# Revit family: Regadera H-3301-CG
name_source: partatom
category: Plumbing Fixtures
revit_build: Autodesk Revit 2015 (Build: 20140223_1515(x64)
units: mm (PartAtom-declared; Revit-internal decimal feet)

## types (1)
- H-3301-C/G
    Ancho = 6.8 "
    Consumo Maximo = 10 l/min
    Default Elevation = 0.5 "
    Description = Regadera redonda de plato ancho, multichorro 7" de 6 chorros.
    Diametro Soporte Base = 2.2 "
    Garantía = El producto HELVEX esta garantizado como libre de defectos en materiales y procesos de fabricacion. El producto HELVEX esta garantizado , en lo que se refiere a los acabados; por un periodo de 10 años en los acabados cromo y duravex, y por 2 años en acabados diferentes al cromo, a partir de la fecha de compra indicada en la factura.
    Largo = 5.3 "
    Manufacturer = HELVEX S.A. DE C.V.
    Material = Brass Chromed
    Model = H-3301-C/G
    Presión máxima de trabajo = 85.3 psi
    Presión mínima de trabajo = 14.2 psi
    Profundidad = 9.6 "
    Type Comments = Regadera Redonda, Multichorro 7"
    Type Image = H-3301-CG.jpg

## geometry (parser evidence)
native form markers: Sweep x6
no freeform markers — native parametric forms only
